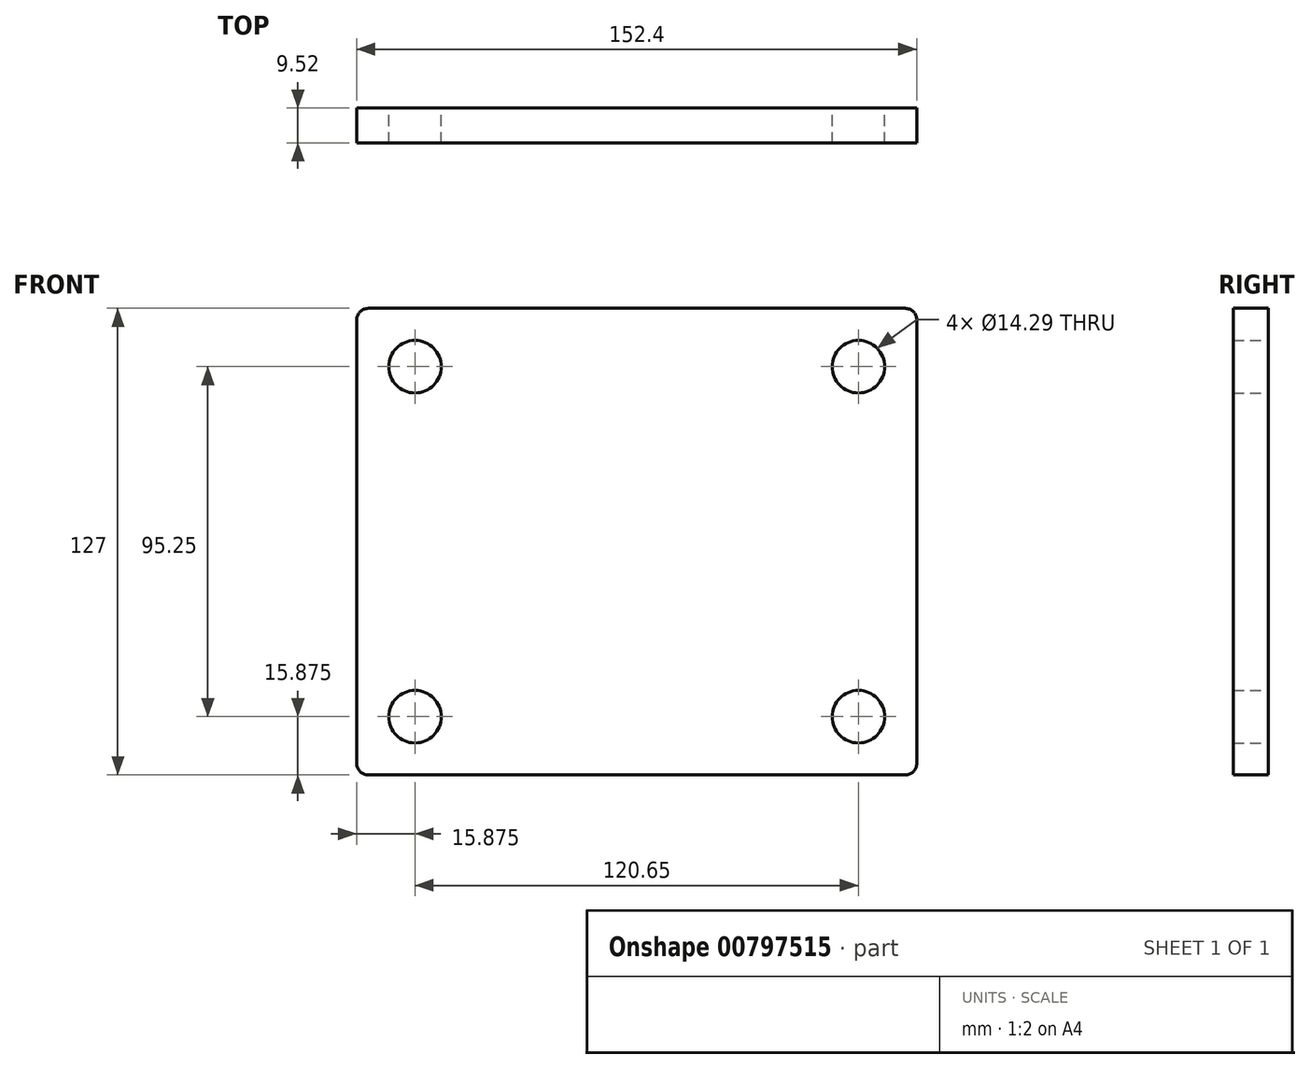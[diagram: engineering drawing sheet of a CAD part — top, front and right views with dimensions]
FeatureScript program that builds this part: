
annotation { "Feature Type Name" : "Feature", "Feature Type Description" : "" }
export const myFeature = defineFeature(function(context is Context, id is Id, definition is map)
    precondition{}
    {
        {
            var Q0;
            Q0=qCreatedBy(makeId("Front.planeOp"),FACE);
            var sketch = newSketch(context, id + "F0", { "sketchPlane" : qUnion([Q0])});
            skLineSegment(sketch, "E0.bottom", {"start": v(73.03, -63.5) * mm, "end": v(-73.03, -63.5) * mm});
            skLineSegment(sketch, "E0.top", {"start": v(73.03, 63.5) * mm, "end": v(-73.03, 63.5) * mm});
            skLineSegment(sketch, "E0.left", {"start": v(76.2, -60.32) * mm, "end": v(76.2, 60.33) * mm});
            skLineSegment(sketch, "E0.right", {"start": v(-76.2, -60.33) * mm, "end": v(-76.2, 60.32) * mm});
            skPoint(sketch, "E0.middle", {"position": v(0, 0) * mm});
            skPoint(sketch, "E1.visualSharp", {"position": v(76.2, 63.5) * mm});
            skArc(sketch, "E1.filletArc", {"start": v(76.2, 60.33) * mm, "mid": v(75.27, 62.57) * mm, "end": v(73.03, 63.5) * mm});
            skPoint(sketch, "E2.visualSharp", {"position": v(76.2, -63.5) * mm});
            skArc(sketch, "E2.filletArc", {"start": v(73.03, -63.5) * mm, "mid": v(75.27, -62.57) * mm, "end": v(76.2, -60.32) * mm});
            skPoint(sketch, "E3.visualSharp", {"position": v(-76.2, -63.5) * mm});
            skArc(sketch, "E3.filletArc", {"start": v(-76.2, -60.33) * mm, "mid": v(-75.27, -62.57) * mm, "end": v(-73.03, -63.5) * mm});
            skPoint(sketch, "E4.visualSharp", {"position": v(-76.2, 63.5) * mm});
            skArc(sketch, "E4.filletArc", {"start": v(-73.03, 63.5) * mm, "mid": v(-75.27, 62.57) * mm, "end": v(-76.2, 60.32) * mm});
            skCircle(sketch, "E5", {"center": v(-60.33, 47.63) * mm, "radius": 7.14 * mm});
            skLineSegment(sketch, "E6", {"start": v(0, 0) * mm, "end": v(0, 85.98) * mm, "construction": true});
            skLineSegment(sketch, "E7", {"start": v(0, 0) * mm, "end": v(100.97, 0) * mm, "construction": true});
            skCircle(sketch, "E8.MirrorC", {"center": v(60.33, 47.63) * mm, "radius": 7.14 * mm});
            skCircle(sketch, "E9.MirrorC", {"center": v(-60.33, -47.63) * mm, "radius": 7.14 * mm});
            skCircle(sketch, "E10.MirrorC", {"center": v(60.33, -47.63) * mm, "radius": 7.14 * mm});
            skSolve(sketch);
        }
        {
            var Q0;
            Q0 = qSketchRegion(id + "F0", true);
            extrude(context, id + "F1", {"entities" : qUnion([Q0]), "endBound" : BoundingType.SYMMETRIC, "depth" : 9.52 * mm, "offsetDistance" : 25.4 * mm});
        }
    });
